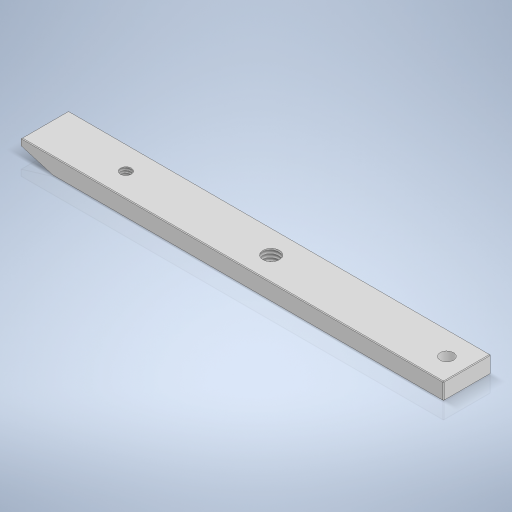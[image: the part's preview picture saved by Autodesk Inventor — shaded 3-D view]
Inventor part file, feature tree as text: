
AUTODESK INVENTOR PART (.ipt)
format: ipt  version: 2024 (Build 280153000, 153)  size: 271,360 bytes
history: native  units: mm
features: sketch x4, hole x3, extrude x1, chamfer x1
ambient origin geometry x8: Origin, YZ Plane, XZ Plane, XY Plane, X Axis, Y Axis, Z Axis, Center Point
bodies: Volumenkörper1 (feature_tree)
feature tree (9):
  extrude  "Extrusion1"  Depth=2.0mm
  hole  "Bohrung1"  [1 undecoded]
  hole  "Bohrung2"  [1 undecoded]
  hole  "Bohrung3"  [1 undecoded]
  chamfer  "Fasen1"  Distance=52.0mm
  sketch  "Skizze1"  dims[d0=10.0mm d1=2.0mm]
  sketch  "Skizze2"  dims[d2=125.0mm d3=5.0mm]
  sketch  "Skizze3"  dims[d4=14.0mm d5=0.0mm]
  sketch  "Skizze4"  dims[d6=3.242mm d7=8.0mm d8=4.0mm d9=2.0mm d10=90.0deg d11=4.5mm d12=0.0mm d13=24.0mm d14=4.917mm d15=12.0mm d16=4.0mm d17=2.0mm d18=90.0deg d19=8.0mm d20=0.0mm d21=43.0mm d22=4.0mm d23=12.0mm d24=4.0mm d25=2.0mm d26=90.0deg d27=8.0mm d28=0.0mm d29=52.0mm d30=6.0mm d31=0.2mm d32=2.0mm d33=45.0deg]
note: 3 required parameter values undecoded (feature->parameter linkage not recoverable at this tier; creation-order binding heuristic only, values carry confidence <= 0.55)
